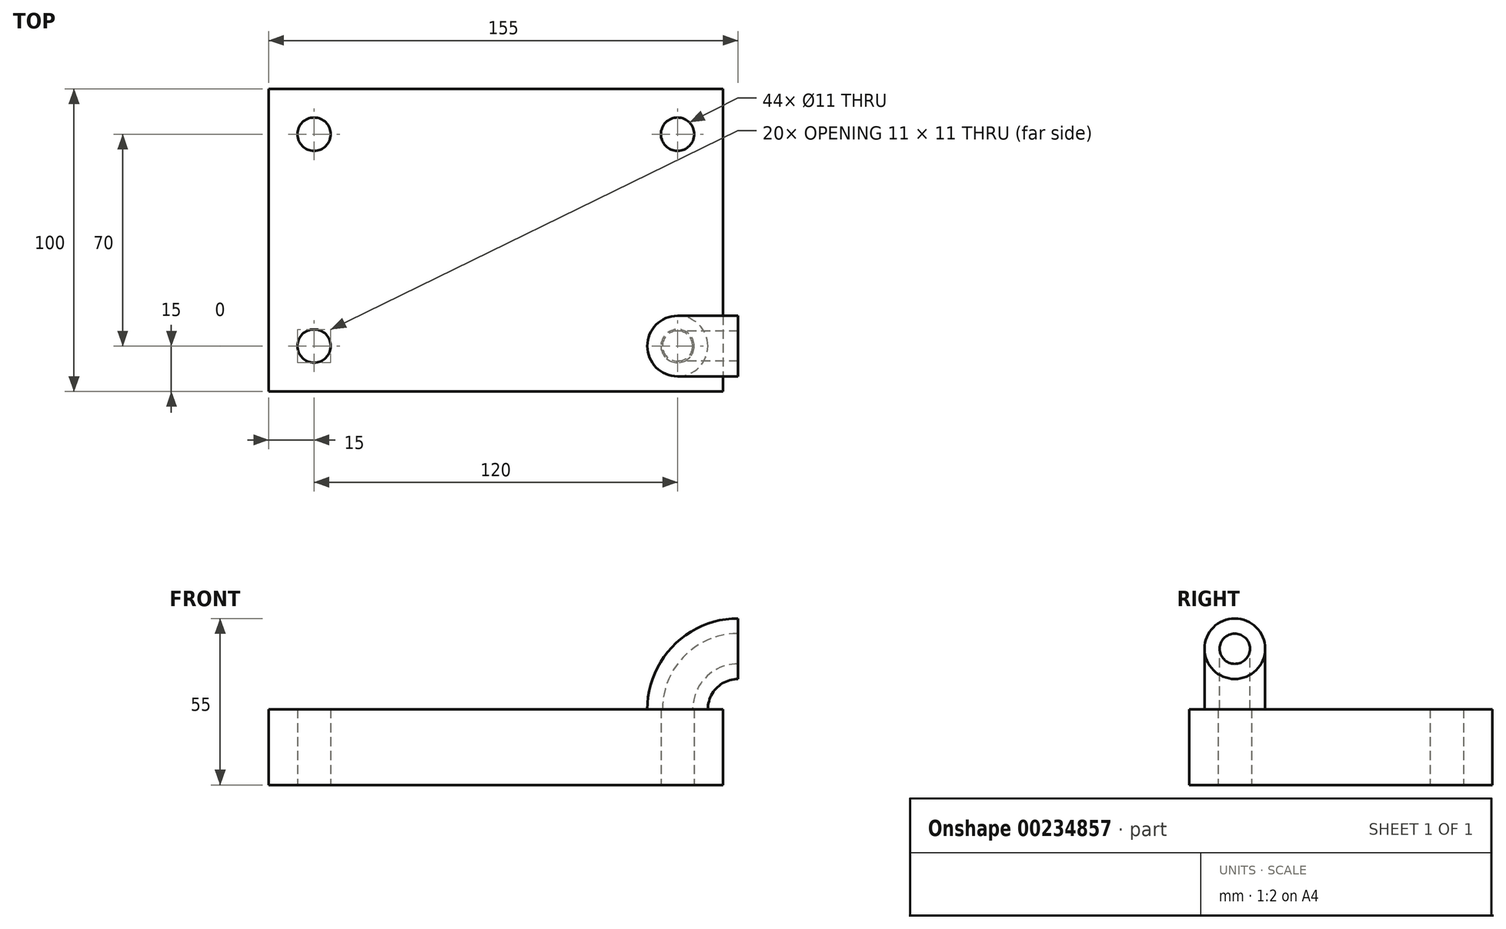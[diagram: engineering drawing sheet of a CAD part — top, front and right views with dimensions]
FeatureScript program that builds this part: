
annotation { "Feature Type Name" : "Feature", "Feature Type Description" : "" }
export const myFeature = defineFeature(function(context is Context, id is Id, definition is map)
    precondition{}
    {
        {
            var Q0;
            Q0=qCreatedBy(makeId("Top.planeOp"),FACE);
            var sketch = newSketch(context, id + "F0", { "sketchPlane" : qUnion([Q0])});
            skLineSegment(sketch, "E0.bottom", {"start": v(75, 50) * mm, "end": v(-75, 50) * mm});
            skLineSegment(sketch, "E0.top", {"start": v(75, -50) * mm, "end": v(-75, -50) * mm});
            skLineSegment(sketch, "E0.left", {"start": v(75, 50) * mm, "end": v(75, -50) * mm});
            skLineSegment(sketch, "E0.right", {"start": v(-75, 50) * mm, "end": v(-75, -50) * mm});
            skPoint(sketch, "E0.middle", {"position": v(0, 0) * mm});
            skLineSegment(sketch, "E1.bottom", {"start": v(60, 35) * mm, "end": v(-60, 35) * mm, "construction": true});
            skLineSegment(sketch, "E1.top", {"start": v(60, -35) * mm, "end": v(-60, -35) * mm, "construction": true});
            skLineSegment(sketch, "E1.left", {"start": v(60, 35) * mm, "end": v(60, -35) * mm, "construction": true});
            skLineSegment(sketch, "E1.right", {"start": v(-60, 35) * mm, "end": v(-60, -35) * mm, "construction": true});
            skSolve(sketch);
        }
        {
            var Q0;
            Q0 = qSketchRegion(id + "F0", true);
            extrude(context, id + "F1", {"entities" : qUnion([Q0]), "oppositeDirection" : true, "depth" : 25 * mm});
        }
        {
            var Q0;
            Q0=sQuery(id+"F0.wireOp",VERTEX,"E1.right.end");
            var Q1;
            Q1=sQuery(id+"F0.wireOp",VERTEX,"E1.left.end");
            var Q2;
            Q2=sQuery(id+"F0.wireOp",VERTEX,"E1.left.start");
            var Q3;
            Q3=sQuery(id+"F0.wireOp",VERTEX,"E1.right.start");
            var Q4;
            Q4=makeQuery(id+"F1.opExtrude","SWEPT_BODY",BODY,{"disambiguationData":[OSD([sQuery(id+"F0.wireOp",EDGE,"E0.bottom"),sQuery(id+"F0.wireOp",EDGE,"E0.top"),sQuery(id+"F0.wireOp",EDGE,"E0.left"),sQuery(id+"F0.wireOp",EDGE,"E0.right")])]});
            hole(context, id + "F2", {"style" : HoleStyle.SIMPLE, "endStyle" : HoleEndStyle.THROUGH, "standardTappedOrClearance" : lookupTablePath({ "standard" : "ISO", "fit" : "Normal", "size" : "M10", "type" : "Clearance" }), "standardBlindInLast" : lookupTablePath({ "fit" : "Standard", "standard" : "ISO", "size" : "M10", "type" : "Clearance" }), "holeDiameter" : 11 * mm, "locations" : qUnion([Q0, Q1, Q2, Q3]), "scope" : qUnion([Q4]), "isTappedThrough" : true, "startStyle" : HoleStartStyle.PART});
        }
        {
            var Q0;
            Q0=makeQuery(id+"F1.opExtrude","CAP_FACE",FACE,{"disambiguationData":[OSD([sQuery(id+"F0.wireOp",EDGE,"E0.bottom"),sQuery(id+"F0.wireOp",EDGE,"E0.top"),sQuery(id+"F0.wireOp",EDGE,"E0.left"),sQuery(id+"F0.wireOp",EDGE,"E0.right")])],"isStart":true});
            var sketch = newSketch(context, id + "F3", { "sketchPlane" : qUnion([Q0])});
            skCircle(sketch, "E2", {"center": v(60, -35) * mm, "radius": 10 * mm});
            skCircle(sketch, "E3", {"center": v(60, -35) * mm, "radius": 5 * mm});
            skLineSegment(sketch, "E4", {"start": v(80, -20.18) * mm, "end": v(80, -49.98) * mm, "construction": true});
            skSolve(sketch);
        }
        {
            var Q0;
            Q0 = qSketchRegion(id + "F3", true);
            var Q1;
            Q1=sQuery(id+"F3.wireOp",EDGE,"E4");
            revolve(context, id + "F4", {"entities" : qUnion([Q0]), "axis" : qUnion([Q1]), "revolveType" : RevolveType.ONE_DIRECTION, "oppositeDirection" : true, "angle" : 90 * degree});
        }
    });
